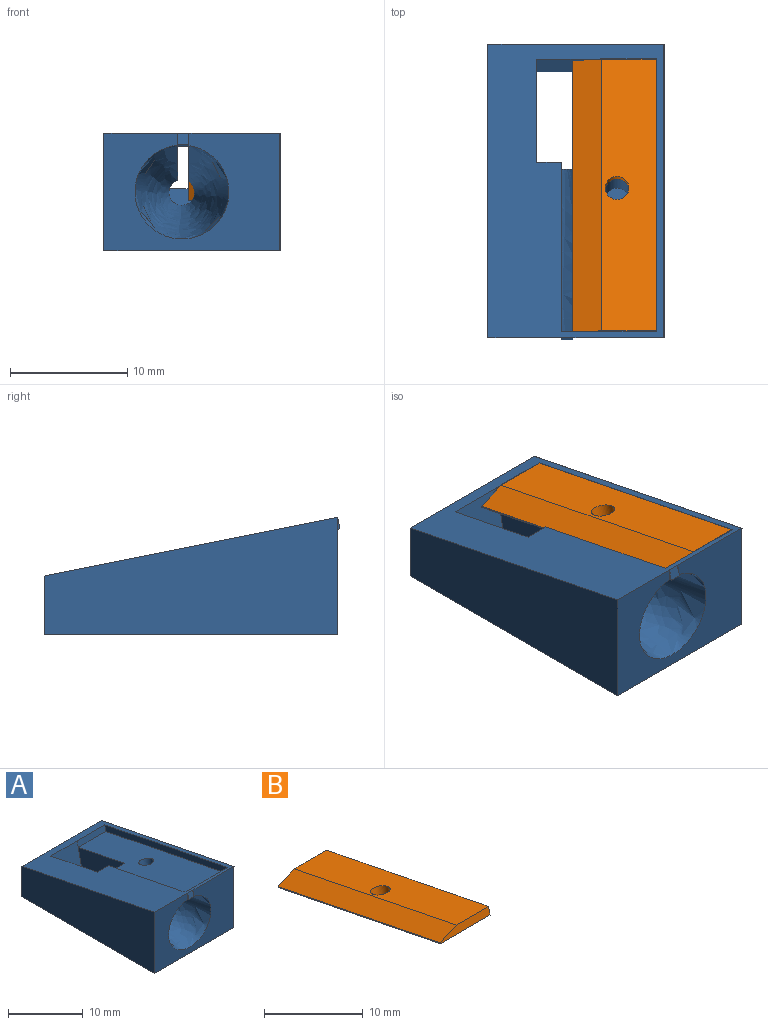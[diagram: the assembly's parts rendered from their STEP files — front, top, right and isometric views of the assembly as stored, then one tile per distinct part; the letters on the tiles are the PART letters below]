
ASSEMBLY  parts=2 mates=1
PART A: 27 faces, bbox 15x25.2x10 mm
  f0: plane 14.77x3.13mm, normal (-1,0,0), area 1mm2, adj f5,f7,f8,f16,f22
  f1: plane 25x14.98mm, normal (0,0.2,0.98), area 172.1mm2, adj f4,f5,f6,f8,f9,f11,f12,f13
  f2: plane 25x14.98mm, normal (0,0,-1), area 328.9mm2, adj f4,f5,f6,f8,f9,f10,f11,f23
  f3: plane 24.95x9.94mm, normal (1,0,0), area 185.9mm2, adj f23,f24,f25,f26
  f4: plane 25x10mm, normal (-1,0,0), area 187.5mm2, adj f1,f2,f5,f6
  f5: plane 14.98x10mm, normal (0,-1,0), area 98.5mm2, adj f0,f1,f2,f4,f7,f19,f20,f24
  f6: plane 14.98x5mm, normal (0,1,0), area 74.9mm2, adj f1,f2,f4,f25
  f7: bspline ~14.75x7.99mm, area 222.5mm2, adj f0,f5,f8,f12,f20
  f8: plane 7.01x5mm, normal (-0.01,0.98,-0.2), area 29mm2, adj f0,f1,f2,f7,f9,f10,f12,f16
  f9: plane 10.19x7.01mm, normal (1,0,0), area 56.1mm2, adj f1,f2,f8,f11
  f10: plane 9.92x6.02mm, normal (-1,0,0), area 46.7mm2, adj f2,f8,f11,f16
  f11: plane 5.26x5mm, normal (0,-0.98,0.2), area 26.8mm2, adj f1,f2,f9,f10,f14
  f12: plane 14.63x3.91mm, normal (1,0,0), area 14.9mm2, adj f1,f7,f8,f15
  f13: plane 23.39x5.62mm, normal (-1,0,0), area 23.7mm2, adj f1,f14,f15,f16
  f14: plane 5.19x0.98mm, normal (0,-0.98,0.2), area 5.2mm2, adj f1,f11,f13,f16
  f15: plane 8.06x0.98mm, normal (0,0.98,-0.2), area 8.1mm2, adj f1,f12,f13,f16,f20,f22
  f16: plane 23.2x7.09mm, normal (0,0.2,0.98), area 147.6mm2, adj f0,f8,f10,f13,f14,f15,f18
  f17: plane 2x1.96mm, normal (0,0.2,0.98), area 3.1mm2, adj f18
  f18: cylinder r=1mm len=4.31mm, axis (0,0.2,0.98), area 25.1mm2, adj f16,f17
  f19: plane 1.02x0.2mm, normal (1,0,0), area 0.1mm2, adj f5,f21,f22
  f20: plane 1.09x0.53mm, normal (-1,0,0), area 0.1mm2, adj f5,f7,f15,f21,f22
  f21: plane 0.98x0.97mm, normal (0,-0.98,0.2), area 1mm2, adj f1,f19,f20,f22
  f22: plane 0.97x0.53mm, normal (0,-0.2,-0.98), area 0.5mm2, adj f0,f15,f19,f20,f21
  f23: cylinder r=0.02mm len=25mm, axis (0,1,0), area 1mm2, adj f2,f3,f24,f25
  f24: cylinder r=0.02mm len=10mm, axis (0,0,-1), area 0.4mm2, adj f3,f5,f23,f26
  f25: cylinder r=0.02mm len=5mm, axis (0,0,1), area 0.2mm2, adj f3,f6,f23,f26
  f26: cylinder r=0.02mm len=25.01mm, axis (0,-0.98,0.2), area 1mm2, adj f1,f3,f24,f25
PART B: 9 faces, bbox 7.1x23.4x5.6 mm
  f0: plane 1.91x0.78mm, normal (0,0.98,-0.2), area 0.9mm2, adj f1,f4,f6,f8
  f1: plane 23.21x4.74mm, normal (-1,0,0), area 2.4mm2, adj f0,f2,f6,f8
  f2: plane 7.1x0.98mm, normal (0,-0.98,0.2), area 6mm2, adj f1,f3,f5,f6,f8
  f3: plane 23.39x5.62mm, normal (1,0,0), area 23.7mm2, adj f2,f4,f5,f6
  f4: plane 5.19x0.98mm, normal (0,0.98,-0.2), area 5.1mm2, adj f0,f3,f5,f6,f8
  f5: plane 23.2x4.64mm, normal (0,0.2,0.98), area 106.3mm2, adj f2,f3,f4,f7,f8
  f6: plane 23.2x7.1mm, normal (0,-0.2,-0.98), area 164.8mm2, adj f0,f1,f2,f3,f4,f7
  f7: cylinder r=1mm len=2.16mm, axis (0,0.2,0.98), area 6.3mm2, adj f5,f6
  f8: plane 23.37x5.52mm, normal (-0.34,0.18,0.92), area 62.2mm2, adj f0,f1,f2,f4,f5
PLACE A rot(axis=(-0.13,0.19,-0.97),0deg) t=(-7.57,-20.68,5.3)mm
PLACE B rot(axis=(-0.13,0.19,-0.97),0deg) t=(-7.58,-20.82,4.31)mm
MATE fastened B.f7 <-> A.f18  axis (0,-0.2,-0.98) through (-4.07,-33.13,6.77)mm
